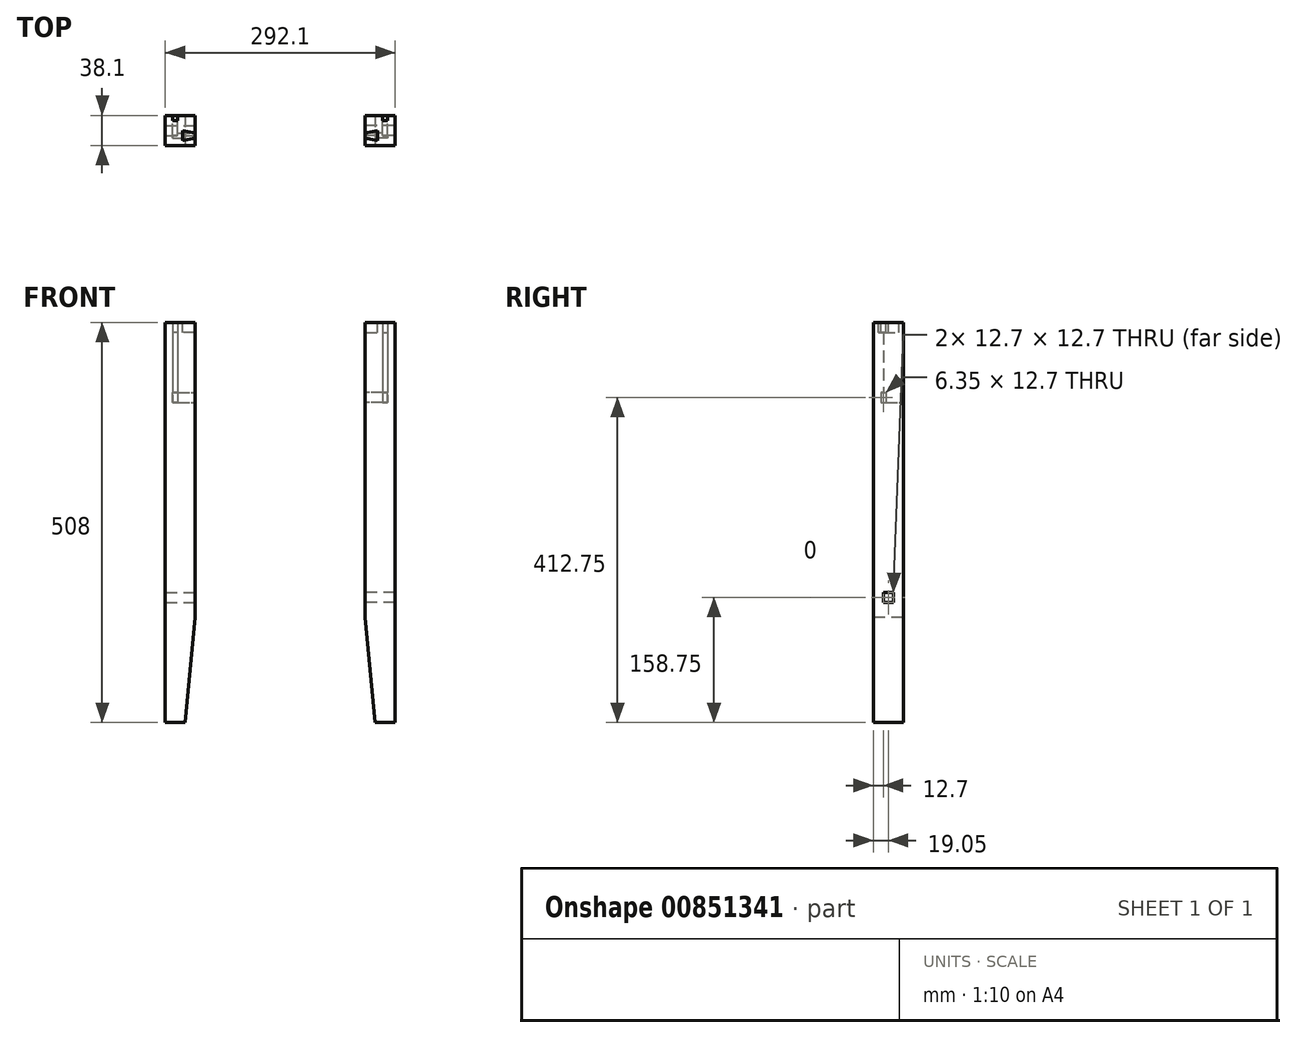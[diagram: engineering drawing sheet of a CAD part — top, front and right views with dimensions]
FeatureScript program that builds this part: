
annotation { "Feature Type Name" : "Feature", "Feature Type Description" : "" }
export const myFeature = defineFeature(function(context is Context, id is Id, definition is map)
    precondition{}
    {
        {
            var Q0;
            Q0=qCreatedBy(makeId("Right.planeOp"),FACE);
            var sketch = newSketch(context, id + "F0", { "sketchPlane" : qUnion([Q0])});
            skLineSegment(sketch, "E0", {"start": v(0, 46.62) * mm, "end": v(0, 24.2) * mm, "construction": true});
            skSolve(sketch);
        }
        {
            var Q0;
            Q0=qCreatedBy(makeId("Right.planeOp"),FACE);
            var Q1;
            Q1=sQuery(id+"F0.wireOp",EDGE,"E0");
            cPlane(context, id + "F1", {"entities" : qUnion([Q0, Q1]), "cplaneType" : CPlaneType.LINE_ANGLE, "offset" : 25.4 * mm, "angle" : 45 * degree, "width" : 152.4 * mm, "height" : 152.4 * mm});
        }
        {
            var Q0;
            Q0=qCreatedBy(makeId("Top.planeOp"),FACE);
            var sketch = newSketch(context, id + "F2", { "sketchPlane" : qUnion([Q0])});
            skLineSegment(sketch, "E1.bottom", {"start": v(-19.05, 19.05) * mm, "end": v(19.05, 19.05) * mm});
            skLineSegment(sketch, "E1.top", {"start": v(-19.05, -19.05) * mm, "end": v(19.05, -19.05) * mm});
            skLineSegment(sketch, "E1.left", {"start": v(-19.05, 19.05) * mm, "end": v(-19.05, -19.05) * mm});
            skLineSegment(sketch, "E1.right", {"start": v(19.05, 19.05) * mm, "end": v(19.05, -19.05) * mm});
            skLineSegment(sketch, "E2", {"start": v(-19.05, 19.05) * mm, "end": v(19.05, -19.05) * mm, "construction": true});
            skSolve(sketch);
        }
        {
            var Q0;
            Q0=qSketchRegion(id+"F2",true);
            extrude(context, id + "F3", {"entities" : qUnion([Q0]), "oppositeDirection" : true, "depth" : 508 * mm, "offsetDistance" : 25.4 * mm});
        }
        {
            var Q0;
            Q0=makeQuery(id+"F3.opExtrude","SWEPT_FACE",FACE,{"disambiguationData":[OSD([sQuery(id+"F2.wireOp",EDGE,"E1.bottom")])]});
            var sketch = newSketch(context, id + "F4", { "sketchPlane" : qUnion([Q0])});
            skLineSegment(sketch, "E3.bottom", {"start": v(3.18, 0) * mm, "end": v(9.53, 0) * mm});
            skLineSegment(sketch, "E3.top", {"start": v(3.18, -101.6) * mm, "end": v(9.53, -101.6) * mm});
            skLineSegment(sketch, "E3.left", {"start": v(3.18, 0) * mm, "end": v(3.18, -101.6) * mm});
            skLineSegment(sketch, "E3.right", {"start": v(9.53, 0) * mm, "end": v(9.53, -101.6) * mm});
            skLineSegment(sketch, "E4", {"start": v(3.18, -12.7) * mm, "end": v(9.53, -12.7) * mm});
            skSolve(sketch);
        }
        {
            var Q0;
            {var subQ0=sQuery(id+"F4.wireOp",EDGE,"E3.top");Q0=makeQuery(id+"F4.imprint","IMPRINT",FACE,{"disambiguationData":[TD([[makeQuery(id+"F4.imprint","IMPRINT",EDGE,{"derivedFrom":subQ0}),1.0]])]});}
            extrude(context, id + "F5", {"entities" : qUnion([Q0]), "operationType" : NewBodyOperationType.REMOVE, "oppositeDirection" : true, "depth" : 25.4 * mm, "offsetDistance" : 25.4 * mm});
        }
        {
            var Q0;
            Q0 = qSketchRegion(id + "F4", true);
            extrude(context, id + "F6", {"entities" : qUnion([Q0]), "operationType" : NewBodyOperationType.REMOVE, "oppositeDirection" : true, "depth" : 6.35 * mm, "offsetDistance" : 25.4 * mm});
        }
        {
            var Q0;
            Q0=makeQuery(id+"F3.opExtrude","SWEPT_FACE",FACE,{"disambiguationData":[OSD([sQuery(id+"F2.wireOp",EDGE,"E1.right")])]});
            var sketch = newSketch(context, id + "F7", { "sketchPlane" : qUnion([Q0])});
            skLineSegment(sketch, "E5", {"start": v(-19.05, -355.6) * mm, "end": v(19.05, -355.6) * mm, "construction": true});
            skLineSegment(sketch, "E6.bottom", {"start": v(-6.35, -342.9) * mm, "end": v(6.35, -342.9) * mm});
            skLineSegment(sketch, "E6.top", {"start": v(-6.35, -355.6) * mm, "end": v(6.35, -355.6) * mm});
            skLineSegment(sketch, "E6.left", {"start": v(-6.35, -342.9) * mm, "end": v(-6.35, -355.6) * mm});
            skLineSegment(sketch, "E6.right", {"start": v(6.35, -342.9) * mm, "end": v(6.35, -355.6) * mm});
            skLineSegment(sketch, "E7", {"start": v(0, -342.9) * mm, "end": v(0, -355.6) * mm, "construction": true});
            skLineSegment(sketch, "E8.bottom", {"start": v(-9.52, -88.9) * mm, "end": v(-3.17, -88.9) * mm});
            skLineSegment(sketch, "E8.top", {"start": v(-9.52, -101.6) * mm, "end": v(-3.17, -101.6) * mm});
            skLineSegment(sketch, "E8.left", {"start": v(-9.52, -88.9) * mm, "end": v(-9.52, -101.6) * mm});
            skLineSegment(sketch, "E8.right", {"start": v(-3.17, -88.9) * mm, "end": v(-3.17, -101.6) * mm});
            skLineSegment(sketch, "E9", {"start": v(-6.35, -88.9) * mm, "end": v(-6.35, -101.6) * mm, "construction": true});
            skSolve(sketch);
        }
        {
            var Q0;
            Q0=makeQuery(id+"F7.imprint","IMPRINT",FACE,{"disambiguationData":[TD([[makeQuery(id+"F7.imprint","IMPRINT",EDGE,{"derivedFrom":sQuery(id+"F7.wireOp",EDGE,"E6.bottom")}),-1.0]])]});
            extrude(context, id + "F8", {"entities" : qUnion([Q0]), "operationType" : NewBodyOperationType.REMOVE, "endBound" : BoundingType.THROUGH_ALL, "oppositeDirection" : true, "depth" : 25.4 * mm, "offsetDistance" : 25.4 * mm});
        }
        {
            var Q0;
            Q0=makeQuery(id+"F7.imprint","IMPRINT",FACE,{"disambiguationData":[TD([[makeQuery(id+"F7.imprint","IMPRINT",EDGE,{"derivedFrom":sQuery(id+"F7.wireOp",EDGE,"E8.bottom")}),-1.0]])]});
            var Q1;
            {var subQ0=sQuery(id+"F4.wireOp",EDGE,"E3.right");Q1=makeQuery(id+"F6.boolean.opBoolean","MERGE",FACE,{"derivedFrom":[makeQuery(id+"F5.boolean.opBoolean","COPY",FACE,{"derivedFrom":makeQuery(id+"F5.opExtrude","SWEPT_FACE",FACE,{"disambiguationData":[OSD([subQ0])]})}),makeQuery(id+"F6.opExtrude","SWEPT_FACE",FACE,{"disambiguationData":[OSD([subQ0])]})]});}
            extrude(context, id + "F9", {"entities" : qUnion([Q0]), "operationType" : NewBodyOperationType.REMOVE, "endBound" : BoundingType.UP_TO_SURFACE, "oppositeDirection" : true, "depth" : 25.4 * mm, "endBoundEntityFace" : qUnion([Q1]), "offsetDistance" : 25.4 * mm});
        }
        {
            var Q0;
            Q0=makeQuery(id+"F3.opExtrude","CAP_FACE",FACE,{"disambiguationData":[OSD([sQuery(id+"F2.wireOp",EDGE,"E1.bottom"),sQuery(id+"F2.wireOp",EDGE,"E1.top"),sQuery(id+"F2.wireOp",EDGE,"E1.left"),sQuery(id+"F2.wireOp",EDGE,"E1.right")])],"isStart":true});
            var sketch = newSketch(context, id + "F10", { "sketchPlane" : qUnion([Q0])});
            skLineSegment(sketch, "E10", {"start": v(19.05, -6.35) * mm, "end": v(-19.05, -6.35) * mm, "construction": true});
            skLineSegment(sketch, "E11.0", {"start": v(19.05, 19.05) * mm, "end": v(19.05, -19.05) * mm});
            skLineSegment(sketch, "E12", {"start": v(19.05, -9.53) * mm, "end": v(3.17, -12.7) * mm});
            skLineSegment(sketch, "E13.MirrorCS", {"start": v(19.05, -3.17) * mm, "end": v(3.17, 0) * mm});
            skLineSegment(sketch, "E14", {"start": v(3.17, -12.7) * mm, "end": v(3.17, 0) * mm});
            skSolve(sketch);
        }
        {
            var Q0;
            Q0 = qSketchRegion(id + "F10", true);
            extrude(context, id + "F11", {"entities" : qUnion([Q0]), "operationType" : NewBodyOperationType.REMOVE, "oppositeDirection" : true, "depth" : 12.7 * mm, "offsetDistance" : 25.4 * mm});
        }
        {
            var Q0;
            Q0=makeQuery(id+"F3.opExtrude","SWEPT_FACE",FACE,{"disambiguationData":[OSD([sQuery(id+"F2.wireOp",EDGE,"E1.top")])]});
            var sketch = newSketch(context, id + "F12", { "sketchPlane" : qUnion([Q0])});
            skLineSegment(sketch, "E15", {"start": v(-19.05, -374.65) * mm, "end": v(19.05, -374.65) * mm, "construction": true});
            skLineSegment(sketch, "E16", {"start": v(19.05, -374.65) * mm, "end": v(6.35, -508) * mm});
            skLineSegment(sketch, "E17.0", {"start": v(6.35, -508) * mm, "end": v(19.05, -508) * mm});
            skLineSegment(sketch, "E18.0", {"start": v(19.05, -508) * mm, "end": v(19.05, -374.65) * mm});
            skPoint(sketch, "E19.orphan", {"position": v(19.05, 0) * mm});
            skSolve(sketch);
        }
        {
            var Q0;
            Q0=qSketchRegion(id+"F12",true);
            extrude(context, id + "F13", {"entities" : qUnion([Q0]), "operationType" : NewBodyOperationType.REMOVE, "endBound" : BoundingType.THROUGH_ALL, "oppositeDirection" : true, "depth" : 25.4 * mm, "offsetDistance" : 25.4 * mm});
        }
        {
            var Q0;
            Q0=qCreatedBy(makeId("Right.planeOp"),FACE);
            cPlane(context, id + "F14", {"entities" : qUnion([Q0]), "cplaneType" : CPlaneType.OFFSET, "offset" : 127 * mm, "width" : 152.4 * mm, "height" : 152.4 * mm});
        }
        {
            var Q0;
            Q0=makeQuery(id+"F3.opExtrude","SWEPT_BODY",BODY,{"disambiguationData":[OSD([sQuery(id+"F2.wireOp",EDGE,"E1.bottom"),sQuery(id+"F2.wireOp",EDGE,"E1.top"),sQuery(id+"F2.wireOp",EDGE,"E1.left"),sQuery(id+"F2.wireOp",EDGE,"E1.right")])]});
            var Q1;
            Q1=qCreatedBy(id+"F14.planeOp",FACE);
            mirror(context, id + "F15", {"entities" : qUnion([Q0]), "mirrorPlane" : qUnion([Q1])});
        }
    });
